# Revit family: QF_MOFFAT_BLUESEAL_CE_GE505D
name_source: partatom
category: Specialty Equipment
revit_build: Autodesk Revit Architecture 2012 (Build: 20110916_2132(x64)
units: mm (PartAtom-declared; Revit-internal decimal feet)

## types (1)
- QF_MOFFAT_BLUESEAL_CE_GE505D
    Apparent Power = 0 VA
    Conn Conduit = Yes
    Cycle = 50 Hz
    Depth = 812 mm  [stored 2.66404 ft]
    Description = 750MM GAS RANGE WITH ELECTRIC STATIC OVEN
    Elec Conn Connection Height = 0 mm  [stored 0 ft]
    Elec Conn RI Height = 0 mm  [stored 0 ft]
    Electrical Remarks = 7.8A PER PHASE
    FL Amps = 8 A
    Gas Connection Height = 0 mm  [stored 0 ft]
    Gas Size = 1"
    Height = 1085 mm
    Manufacturer = MOFFAT BLUESEAL
    Max Overcurrent Protection = 0 A
    Min Ckt Ampacity = 0 A
    Model = GE505D
    Phase = 3
    URL = www.moffat.com
    URL Cutsheet = www.moffat.com
    Volts = 400 V
    Watts = 5500 W
    Weight in Pounds = 401
    Width = 750 mm  [stored 2.46063 ft]

note: [stored X ft] marks values corroborated as IEEE doubles in the binary element streams (Revit-internal decimal feet)

## geometry (parser evidence)
native form markers: Blend x7, Sweep x3
no freeform markers — native parametric forms only
